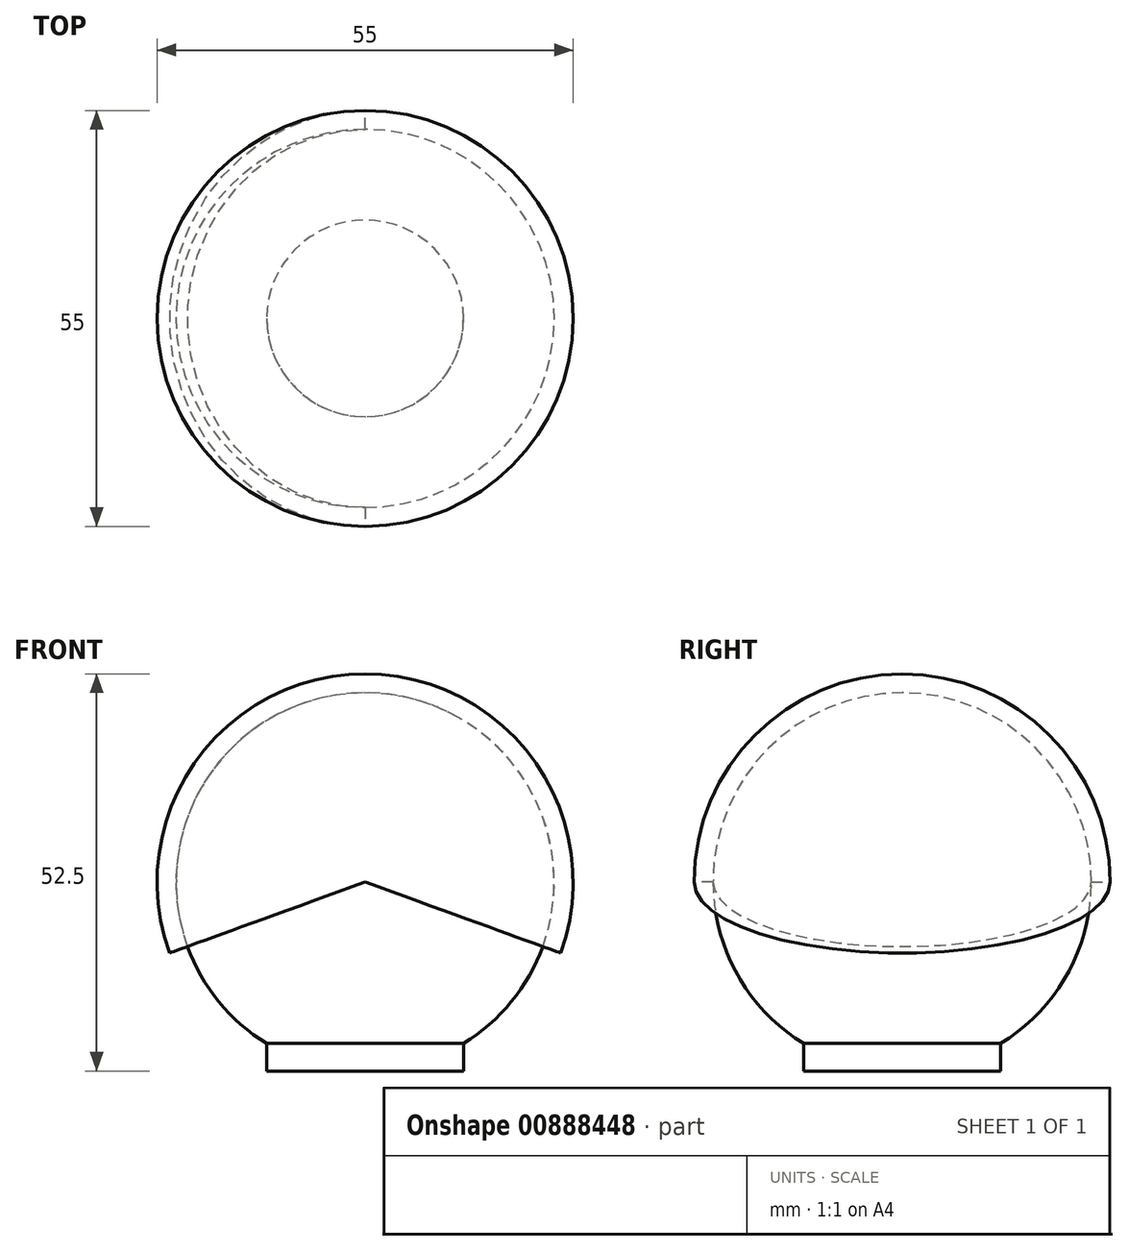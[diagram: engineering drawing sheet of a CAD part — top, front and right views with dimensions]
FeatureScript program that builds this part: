
annotation { "Feature Type Name" : "Feature", "Feature Type Description" : "" }
export const myFeature = defineFeature(function(context is Context, id is Id, definition is map)
    precondition{}
    {
        {
            var Q0;
            Q0=qCreatedBy(makeId("Top.planeOp"),FACE);
            var sketch = newSketch(context, id + "F0", { "sketchPlane" : qUnion([Q0])});
            skCircle(sketch, "E0", {"center": v(0, 0) * mm, "radius": 10 * mm});
            skSolve(sketch);
        }
        {
            var Q0;
            Q0 = qSketchRegion(id + "F0", true);
            extrude(context, id + "F1", {"entities" : qUnion([Q0]), "depth" : 6 * mm, "offsetDistance" : 25 * mm});
        }
        {
            var Q0;
            Q0=makeQuery(id+"F1.opExtrude","CAP_FACE",FACE,{"disambiguationData":[OSD([sQuery(id+"F0.wireOp",EDGE,"E0")])],"isStart":true});
            var sketch = newSketch(context, id + "F2", { "sketchPlane" : qUnion([Q0])});
            skCircle(sketch, "E1", {"center": v(0, 0) * mm, "radius": 13 * mm});
            skSolve(sketch);
        }
        {
            var Q0;
            Q0 = qSketchRegion(id + "F2", true);
            extrude(context, id + "F3", {"entities" : qUnion([Q0]), "oppositeDirection" : true, "depth" : 25 * mm, "offsetDistance" : 25 * mm});
        }
        {
            var Q0;
            Q0=makeQuery(id+"F1.opExtrude","SWEPT_BODY",BODY,{"disambiguationData":[OSD([sQuery(id+"F0.wireOp",EDGE,"E0")])]});
            var Q1;
            Q1=makeQuery(id+"F3.opExtrude","SWEPT_BODY",BODY,{"disambiguationData":[OSD([sQuery(id+"F2.wireOp",EDGE,"E1")])]});
            booleanBodies(context, id + "F4", {"operationType" : BooleanOperationType.SUBTRACTION, "tools" : qUnion([Q0]), "targets" : qUnion([Q1]), "keepTools" : true});
        }
        {
            var Q0;
            Q0=makeQuery(id+"F3.opExtrude","CAP_FACE",FACE,{"disambiguationData":[OSD([sQuery(id+"F2.wireOp",EDGE,"E1")])],"isStart":false});
            var sketch = newSketch(context, id + "F5", { "sketchPlane" : qUnion([Q0])});
            skLineSegment(sketch, "E2", {"start": v(0, 25) * mm, "end": v(0, -25) * mm});
            skArc(sketch, "E3", {"start": v(0, -25) * mm, "mid": v(25, 0) * mm, "end": v(0, 25) * mm});
            skArc(sketch, "E4.0", {"start": v(0, -27.5) * mm, "mid": v(27.5, 0) * mm, "end": v(0, 27.5) * mm});
            skLineSegment(sketch, "E5", {"start": v(0, 25) * mm, "end": v(0, 27.5) * mm});
            skLineSegment(sketch, "E6", {"start": v(0, -25) * mm, "end": v(0, -27.5) * mm});
            skSolve(sketch);
        }
        {
            var Q0;
            {var subQ0=sQuery(id+"F5.wireOp",EDGE,"E2");var subQ1=makeQuery(id+"F3.opExtrude","CAP_EDGE",EDGE,{"disambiguationData":[OSD([sQuery(id+"F2.wireOp",EDGE,"E1")])],"isStart":false});var subQ2=makeQuery(id+"F5.imprint","INTERSECT",VERTEX,{"disambiguationData":[OD(0.0)],"derivedFrom":[subQ1,subQ0]});Q0=makeQuery(id+"F5.imprint","IMPRINT",FACE,{"disambiguationData":[TD([[makeQuery(id+"F5.imprint","IMPRINT",EDGE,{"disambiguationData":[TD([[subQ2,-1.0]])],"derivedFrom":subQ0}),1.0]])]});}
            var Q1;
            {var subQ0=sQuery(id+"F5.wireOp",EDGE,"E3");Q1=makeQuery(id+"F5.imprint","IMPRINT",FACE,{"disambiguationData":[TD([[makeQuery(id+"F5.imprint","IMPRINT",EDGE,{"derivedFrom":subQ0}),1.0]])]});}
            var Q2;
            Q2=sQuery(id+"F5.wireOp",EDGE,"E2");
            revolve(context, id + "F6", {"operationType" : NewBodyOperationType.ADD, "surfaceOperationType" : NewSurfaceOperationType.NEW, "entities" : qUnion([Q0, Q1]), "axis" : qUnion([Q2]), "revolveType" : RevolveType.FULL});
        }
        {
            var Q0;
            Q0=makeQuery(id+"F5.imprint","IMPRINT",FACE,{"disambiguationData":[TD([[makeQuery(id+"F5.imprint","IMPRINT",EDGE,{"derivedFrom":sQuery(id+"F5.wireOp",EDGE,"E3")}),-1.0]])]});
            var Q1;
            Q1=sQuery(id+"F5.wireOp",EDGE,"E2");
            revolve(context, id + "F7", {"surfaceOperationType" : NewSurfaceOperationType.NEW, "entities" : qUnion([Q0]), "axis" : qUnion([Q1]), "revolveType" : RevolveType.ONE_DIRECTION, "angle" : 220 * degree});
        }
        {
            var Q0;
            Q0=makeQuery(id+"F7.opRevolve","SWEPT_BODY",BODY,{"disambiguationData":[OSD([sQuery(id+"F5.wireOp",EDGE,"E3"),sQuery(id+"F5.wireOp",EDGE,"E4.0"),sQuery(id+"F5.wireOp",EDGE,"E5"),sQuery(id+"F5.wireOp",EDGE,"E6")])]});
            var Q1;
            Q1=sQuery(id+"F5.wireOp",EDGE,"E2");
            transform(context, id + "F8", {"entities" : qUnion([Q0]), "transformType" : TransformType.ROTATION, "transformAxis" : qUnion([Q1]), "angle" : 20 * degree, "oppositeDirection" : true, "makeCopy" : false});
        }
    });
